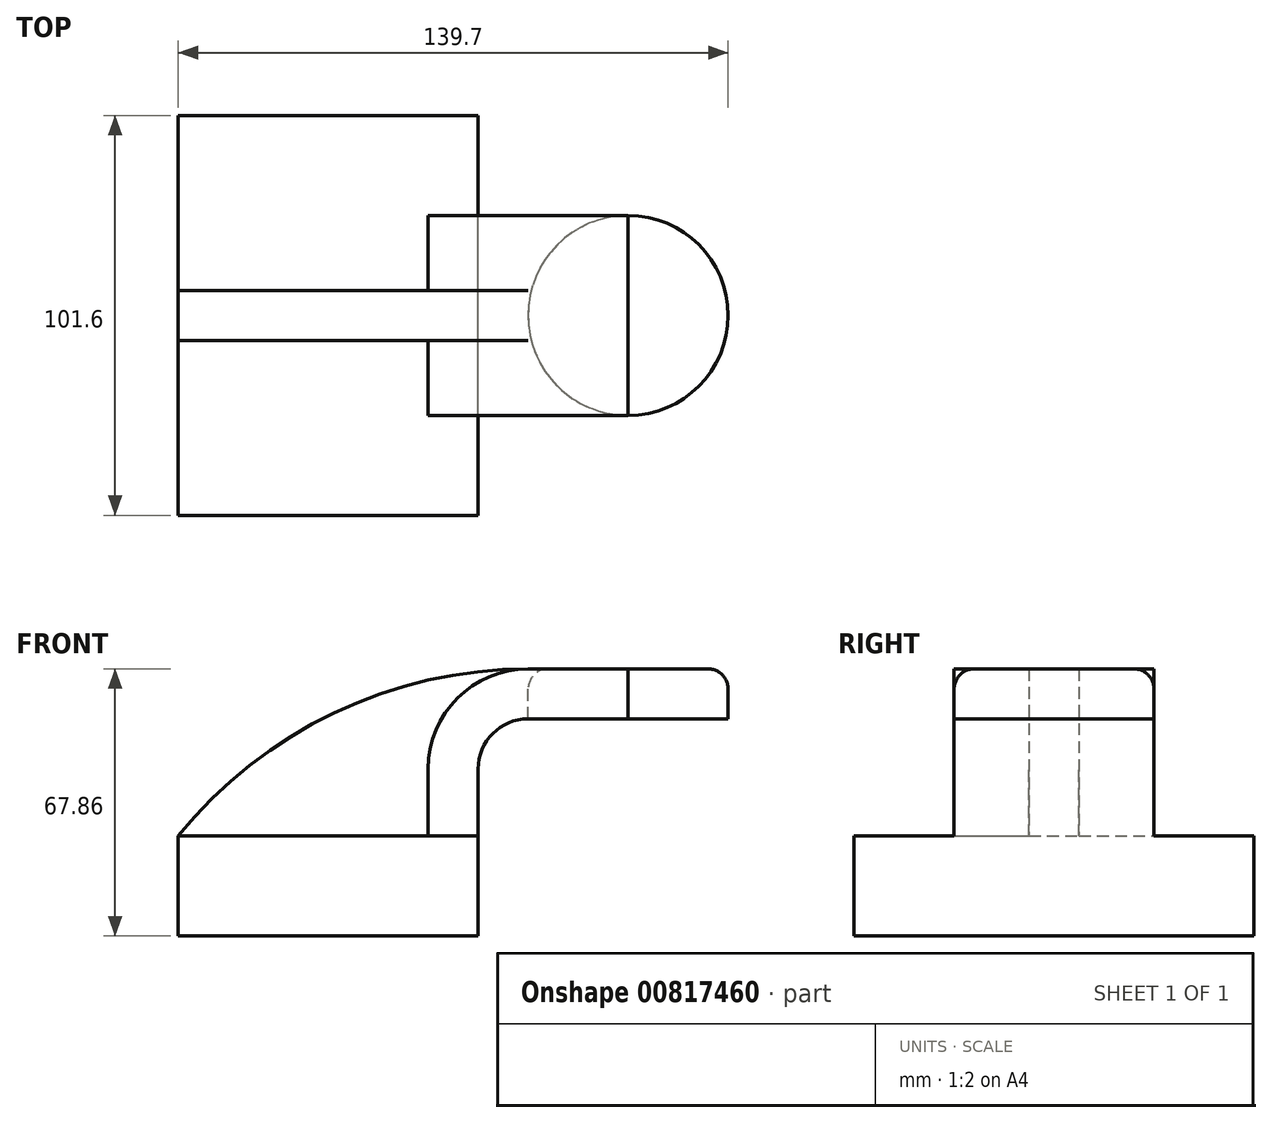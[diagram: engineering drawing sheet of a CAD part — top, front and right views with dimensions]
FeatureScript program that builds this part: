
annotation { "Feature Type Name" : "Feature", "Feature Type Description" : "" }
export const myFeature = defineFeature(function(context is Context, id is Id, definition is map)
    precondition{}
    {
        {
            var Q0;
            Q0=qCreatedBy(makeId("Front.planeOp"),FACE);
            var sketch = newSketch(context, id + "F0", { "sketchPlane" : qUnion([Q0])});
            skLineSegment(sketch, "E0.bottom", {"start": v(-38.1, -12.7) * mm, "end": v(38.1, -12.7) * mm});
            skLineSegment(sketch, "E0.top", {"start": v(-38.1, 12.7) * mm, "end": v(38.1, 12.7) * mm});
            skLineSegment(sketch, "E0.left", {"start": v(-38.1, -12.7) * mm, "end": v(-38.1, 12.7) * mm});
            skLineSegment(sketch, "E0.right", {"start": v(38.1, -12.7) * mm, "end": v(38.1, 12.7) * mm});
            skPoint(sketch, "E0.middle", {"position": v(0, 0) * mm});
            skLineSegment(sketch, "E1.bottom", {"start": v(50.8, 29.76) * mm, "end": v(101.6, 29.76) * mm});
            skLineSegment(sketch, "E1.top", {"start": v(50.8, 55.16) * mm, "end": v(101.6, 55.16) * mm});
            skLineSegment(sketch, "E1.left", {"start": v(50.8, 29.76) * mm, "end": v(50.8, 55.16) * mm});
            skLineSegment(sketch, "E1.right", {"start": v(101.6, 29.76) * mm, "end": v(101.6, 55.16) * mm});
            skPoint(sketch, "E1.middle", {"position": v(76.2, 42.46) * mm});
            skLineSegment(sketch, "E2", {"start": v(38.1, 12.7) * mm, "end": v(38.1, 29.76) * mm});
            skPoint(sketch, "E3.visualSharp", {"position": v(38.1, 12.7) * mm});
            skArc(sketch, "E4", {"start": v(38.1, 29.76) * mm, "mid": v(41.82, 38.74) * mm, "end": v(50.8, 42.46) * mm});
            skLineSegment(sketch, "E5", {"start": v(50.8, 42.46) * mm, "end": v(76.2, 42.46) * mm});
            skLineSegment(sketch, "E6.0", {"start": v(50.8, 55.16) * mm, "end": v(76.2, 55.16) * mm});
            skArc(sketch, "E6.1", {"start": v(25.4, 29.76) * mm, "mid": v(32.84, 47.72) * mm, "end": v(50.8, 55.16) * mm});
            skLineSegment(sketch, "E6.2", {"start": v(25.4, 12.7) * mm, "end": v(25.4, 29.76) * mm});
            skArc(sketch, "E7", {"start": v(50.8, 55.16) * mm, "mid": v(1.54, 44) * mm, "end": v(-38.1, 12.7) * mm});
            skPoint(sketch, "E8", {"position": v(32.84, 47.72) * mm});
            skLineSegment(sketch, "E9", {"start": v(76.2, 55.16) * mm, "end": v(76.2, 29.76) * mm});
            skSolve(sketch);
        }
        {
            var Q0;
            {var subQ1=sQuery(id+"F0.wireOp",EDGE,"E2");Q0=makeQuery(id+"F0.imprint","IMPRINT",FACE,{"disambiguationData":[TD([[makeQuery(id+"F0.imprint","IMPRINT",EDGE,{"derivedFrom":subQ1}),1.0]])]});}
            var Q1;
            {var subQ2=sQuery(id+"F0.wireOp",EDGE,"E5");Q1=makeQuery(id+"F0.imprint","IMPRINT",FACE,{"disambiguationData":[TD([[makeQuery(id+"F0.imprint","IMPRINT",EDGE,{"derivedFrom":subQ2}),1.0]])]});}
            extrude(context, id + "F1", {"entities" : qUnion([Q0, Q1]), "endBound" : BoundingType.SYMMETRIC, "depth" : 50.8 * mm, "offsetDistance" : 25.4 * mm, "hasSecondDirection" : true, "secondDirectionOppositeDirection" : true, "secondDirectionDepth" : 12.7 * mm});
        }
        {
            var Q0;
            {var subQ3=sQuery(id+"F0.wireOp",EDGE,"E6.2");Q0=makeQuery(id+"F0.imprint","IMPRINT",FACE,{"disambiguationData":[TD([[makeQuery(id+"F0.imprint","IMPRINT",EDGE,{"derivedFrom":subQ3}),1.0]])]});}
            extrude(context, id + "F2", {"entities" : qUnion([Q0]), "operationType" : NewBodyOperationType.ADD, "depth" : 6.35 * mm, "offsetDistance" : 25.4 * mm, "hasSecondDirection" : true, "secondDirectionOppositeDirection" : true, "secondDirectionDepth" : 6.35 * mm});
        }
        {
            var Q0;
            Q0=makeQuery(id+"F0.imprint","IMPRINT",FACE,{"disambiguationData":[TD([[makeQuery(id+"F0.imprint","IMPRINT",EDGE,{"derivedFrom":sQuery(id+"F0.wireOp",EDGE,"E0.bottom")}),1.0]])]});
            extrude(context, id + "F3", {"entities" : qUnion([Q0]), "operationType" : NewBodyOperationType.ADD, "depth" : 50.8 * mm, "offsetDistance" : 25.4 * mm, "hasSecondDirection" : true, "secondDirectionOppositeDirection" : true, "secondDirectionDepth" : 50.8 * mm});
        }
        {
            var Q0;
            {var subQ1=sQuery(id+"F0.wireOp",EDGE,"E1.top");Q0=makeQuery(id+"F0.imprint","IMPRINT",FACE,{"disambiguationData":[TD([[makeQuery(id+"F0.imprint","IMPRINT",EDGE,{"derivedFrom":subQ1}),-1.0]])]});}
            var Q1;
            Q1=sQuery(id+"F0.wireOp",EDGE,"E9");
            revolve(context, id + "F4", {"surfaceOperationType" : NewSurfaceOperationType.NEW, "entities" : qUnion([Q0]), "axis" : qUnion([Q1]), "revolveType" : RevolveType.FULL});
        }
        {
            var Q0;
            Q0=makeQuery(id+"F3.opExtrude","CAP_EDGE",EDGE,{"disambiguationData":[OSD([sQuery(id+"F0.wireOp",EDGE,"E0.top")])],"isStart":false});
            var Q1;
            {var subQ0=sQuery(id+"F0.wireOp",EDGE,"E0.top");var subQ1=sQuery(id+"F0.wireOp",EDGE,"E0.right");var subQ2=sQuery(id+"F0.wireOp",EDGE,"E2");Q1=makeQuery(id+"F3.boolean.opBoolean","SPLIT",EDGE,{"disambiguationData":[TD([makeQuery(id+"F3.opExtrude","CAP_FACE",FACE,{"disambiguationData":[OSD([sQuery(id+"F0.wireOp",EDGE,"E0.bottom"),subQ0,sQuery(id+"F0.wireOp",EDGE,"E0.left"),subQ1])],"isStart":false})])],"derivedFrom":makeQuery(id+"F3.opExtrude","SWEPT_EDGE",EDGE,{"disambiguationData":[OSD([subQ0,subQ1,subQ2])]})});}
            var Q2;
            Q2=makeQuery(id+"F3.opExtrude","CAP_EDGE",EDGE,{"disambiguationData":[OSD([sQuery(id+"F0.wireOp",EDGE,"E0.right")])],"isStart":false});
            var Q3;
            Q3=makeQuery(id+"F3.opExtrude","CAP_EDGE",EDGE,{"disambiguationData":[OSD([sQuery(id+"F0.wireOp",EDGE,"E0.bottom")])],"isStart":false});
            var Q4;
            Q4=makeQuery(id+"F3.opExtrude","CAP_EDGE",EDGE,{"disambiguationData":[OSD([sQuery(id+"F0.wireOp",EDGE,"E0.left")])],"isStart":false});
            var Q5;
            Q5=makeQuery(id+"F3.opExtrude","SWEPT_EDGE",EDGE,{"disambiguationData":[OSD([sQuery(id+"F0.wireOp",EDGE,"E0.bottom"),sQuery(id+"F0.wireOp",EDGE,"E0.left")])]});
            var Q6;
            {var subQ0=sQuery(id+"F0.wireOp",EDGE,"E7");var subQ1=sQuery(id+"F0.wireOp",EDGE,"E0.left");var subQ2=sQuery(id+"F0.wireOp",EDGE,"E0.top");Q6=makeQuery(id+"F3.boolean.opBoolean","MERGE",EDGE,{"derivedFrom":[makeQuery(id+"F2.opExtrude","SWEPT_EDGE",EDGE,{"disambiguationData":[OSD([subQ2,subQ1,subQ0])]}),makeQuery(id+"F3.opExtrude","SWEPT_EDGE",EDGE,{"disambiguationData":[OSD([subQ2,subQ1,subQ0])]})]});}
            var Q7;
            Q7=makeQuery(id+"F1.opExtrude","CAP_EDGE",EDGE,{"disambiguationData":[OSD([sQuery(id+"F0.wireOp",EDGE,"E4")])],"isStart":false});
            var Q8;
            Q8=makeQuery(id+"F1.opExtrude","CAP_EDGE",EDGE,{"disambiguationData":[OSD([sQuery(id+"F0.wireOp",EDGE,"E2")])],"isStart":false});
            var Q9;
            Q9=makeQuery(id+"F1.opExtrude","CAP_EDGE",EDGE,{"disambiguationData":[OSD([sQuery(id+"F0.wireOp",EDGE,"E6.2")])],"isStart":false});
            var Q10;
            Q10=makeQuery(id+"F4.opRevolve","SWEPT_EDGE",EDGE,{"disambiguationData":[OSD([sQuery(id+"F0.wireOp",EDGE,"E1.top"),sQuery(id+"F0.wireOp",EDGE,"E1.right")])]});
            var Q11;
            Q11=makeQuery(id+"F4.opRevolve","SWEPT_EDGE",EDGE,{"disambiguationData":[OSD([sQuery(id+"F0.wireOp",EDGE,"E1.bottom"),sQuery(id+"F0.wireOp",EDGE,"E1.right")])]});
            var Q12;
            Q12=makeQuery(id+"F1.opExtrude","CAP_EDGE",EDGE,{"disambiguationData":[OSD([sQuery(id+"F0.wireOp",EDGE,"E4")])],"isStart":true});
            var Q13;
            Q13=makeQuery(id+"F1.opExtrude","CAP_EDGE",EDGE,{"disambiguationData":[OSD([sQuery(id+"F0.wireOp",EDGE,"E6.1")])],"isStart":true});
            var Q14;
            Q14=makeQuery(id+"F3.opExtrude","CAP_EDGE",EDGE,{"disambiguationData":[OSD([sQuery(id+"F0.wireOp",EDGE,"E0.top")])],"isStart":true});
            var Q15;
            {var subQ0=sQuery(id+"F0.wireOp",EDGE,"E0.right");var subQ1=sQuery(id+"F0.wireOp",EDGE,"E0.top");var subQ2=sQuery(id+"F0.wireOp",EDGE,"E2");Q15=makeQuery(id+"F3.boolean.opBoolean","SPLIT",EDGE,{"disambiguationData":[TD([makeQuery(id+"F3.opExtrude","CAP_FACE",FACE,{"disambiguationData":[OSD([sQuery(id+"F0.wireOp",EDGE,"E0.bottom"),subQ1,sQuery(id+"F0.wireOp",EDGE,"E0.left"),subQ0])],"isStart":true})])],"derivedFrom":makeQuery(id+"F3.opExtrude","SWEPT_EDGE",EDGE,{"disambiguationData":[OSD([subQ1,subQ0,subQ2])]})});}
            var Q16;
            Q16=makeQuery(id+"F3.opExtrude","SWEPT_EDGE",EDGE,{"disambiguationData":[OSD([sQuery(id+"F0.wireOp",EDGE,"E0.bottom"),sQuery(id+"F0.wireOp",EDGE,"E0.right")])]});
            var Q17;
            Q17=makeQuery(id+"F3.opExtrude","CAP_EDGE",EDGE,{"disambiguationData":[OSD([sQuery(id+"F0.wireOp",EDGE,"E0.right")])],"isStart":true});
            var Q18;
            Q18=makeQuery(id+"F3.opExtrude","CAP_EDGE",EDGE,{"disambiguationData":[OSD([sQuery(id+"F0.wireOp",EDGE,"E0.left")])],"isStart":true});
            fillet(context, id + "F5", {"entities" : qUnion([Q0, Q1, Q2, Q3, Q4, Q5, Q6, Q7, Q8, Q9, Q10, Q11, Q12, Q13, Q14, Q15, Q16, Q17, Q18]), "radius" : 5.08 * mm, "tangentPropagation" : true, "allowEdgeOverflow" : false});
        }
    });
